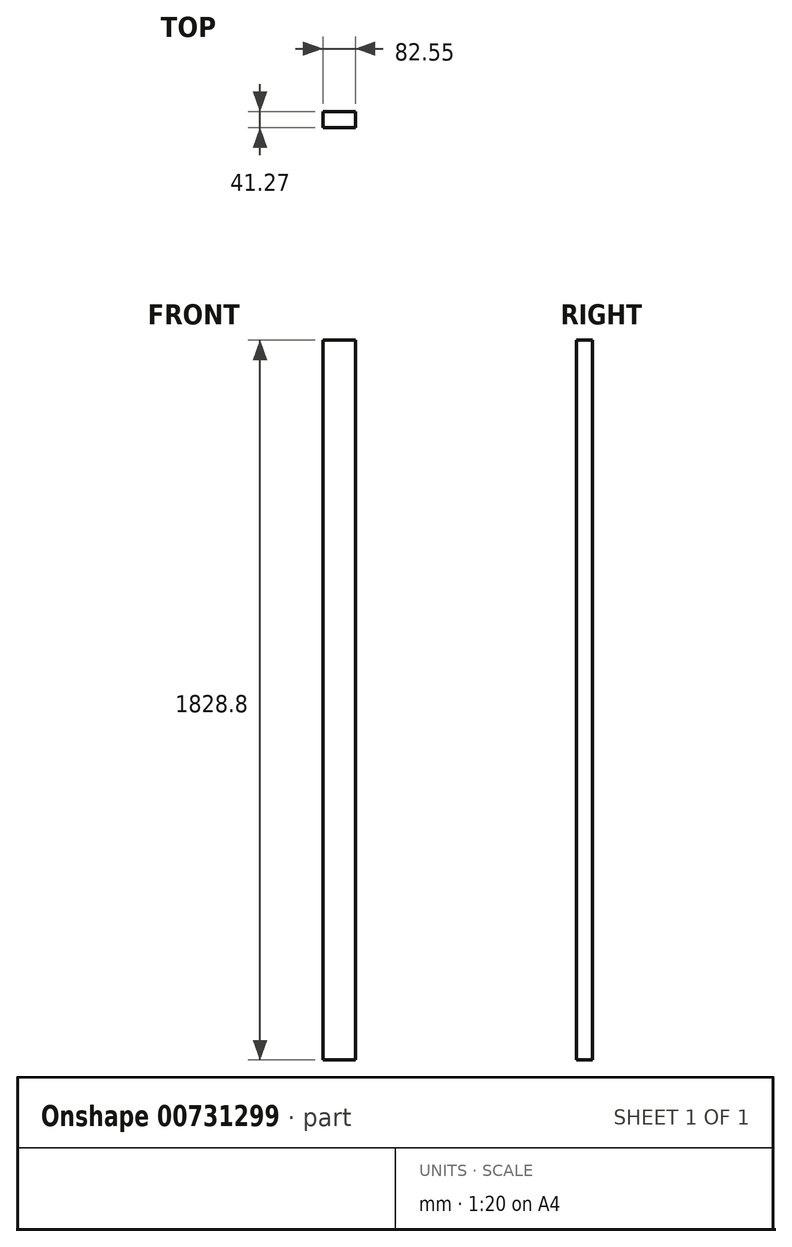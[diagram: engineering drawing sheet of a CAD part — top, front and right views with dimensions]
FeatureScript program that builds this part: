
annotation { "Feature Type Name" : "Feature", "Feature Type Description" : "" }
export const myFeature = defineFeature(function(context is Context, id is Id, definition is map)
    precondition{}
    {
        {
            var Q0;
            Q0=qCreatedBy(makeId("Front.planeOp"),FACE);
            var sketch = newSketch(context, id + "F0", { "sketchPlane" : qUnion([Q0])});
            skLineSegment(sketch, "E0.bottom", {"start": v(0, 0) * mm, "end": v(82.55, 0) * mm});
            skLineSegment(sketch, "E0.top", {"start": v(0, 1828.8) * mm, "end": v(82.55, 1828.8) * mm});
            skLineSegment(sketch, "E0.left", {"start": v(0, 0) * mm, "end": v(0, 1828.8) * mm});
            skLineSegment(sketch, "E0.right", {"start": v(82.55, 0) * mm, "end": v(82.55, 1828.8) * mm});
            skPoint(sketch, "E1", {"position": v(82.55, 609.6) * mm});
            skPoint(sketch, "E2", {"position": v(82.55, 1219.2) * mm});
            skSolve(sketch);
        }
        {
            var Q0;
            Q0=makeQuery(id+"F0.imprint","IMPRINT",FACE,{"disambiguationData":[TD([[makeQuery(id+"F0.imprint","IMPRINT",EDGE,{"derivedFrom":sQuery(id+"F0.wireOp",EDGE,"E0.bottom")}),1.0]])]});
            extrude(context, id + "F1", {"entities" : qUnion([Q0]), "depth" : 41.27 * mm, "offsetDistance" : 25.4 * mm});
        }
    });
